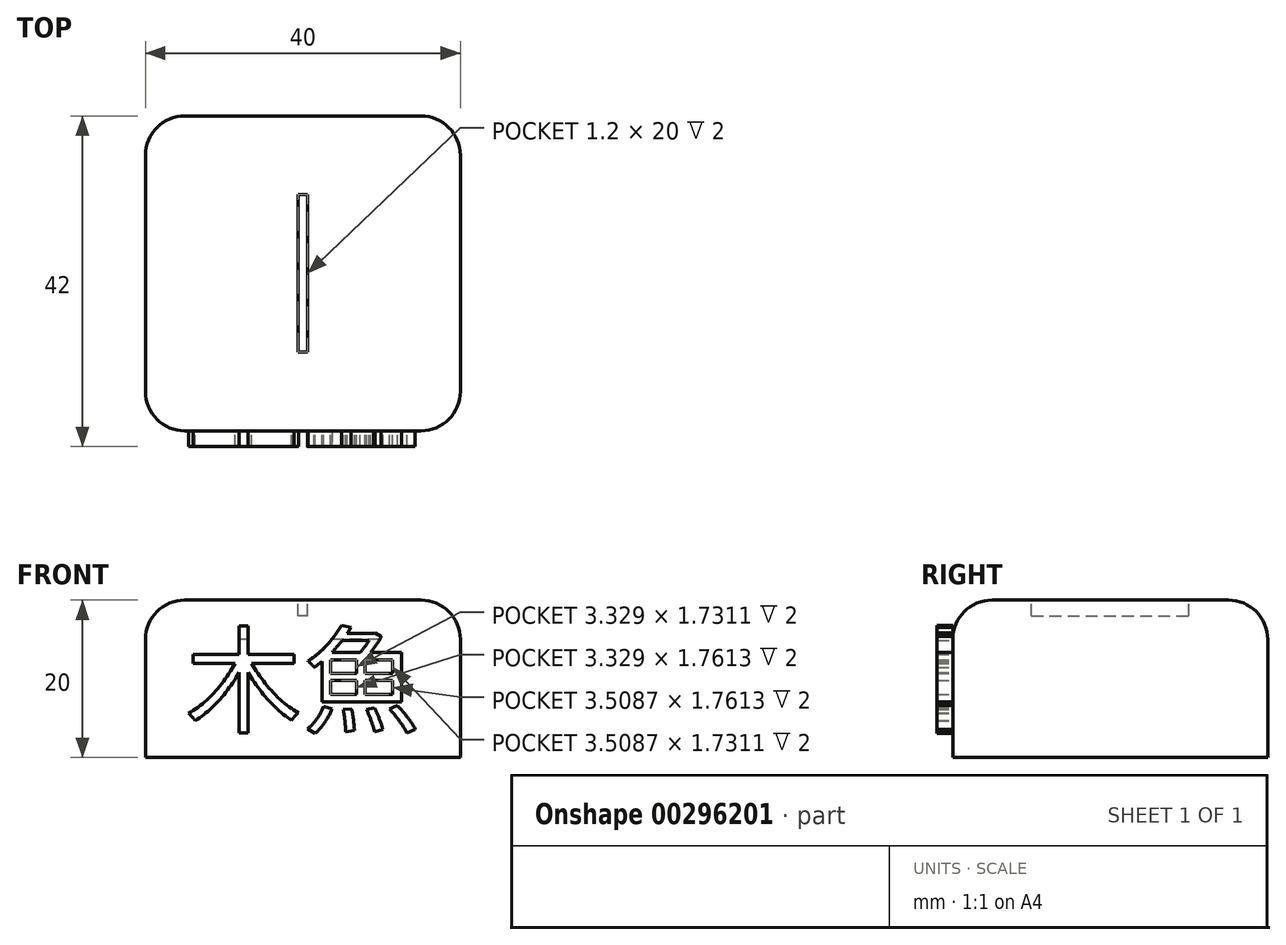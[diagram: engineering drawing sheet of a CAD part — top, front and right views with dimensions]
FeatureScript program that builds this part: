
annotation { "Feature Type Name" : "Feature", "Feature Type Description" : "" }
export const myFeature = defineFeature(function(context is Context, id is Id, definition is map)
    precondition{}
    {
        {
            var Q0;
            Q0=qCreatedBy(makeId("Top.planeOp"),FACE);
            var sketch = newSketch(context, id + "F0", { "sketchPlane" : qUnion([Q0])});
            skLineSegment(sketch, "E0.bottom", {"start": v(20, -20) * mm, "end": v(-20, -20) * mm});
            skLineSegment(sketch, "E0.top", {"start": v(20, 20) * mm, "end": v(-20, 20) * mm});
            skLineSegment(sketch, "E0.left", {"start": v(20, -20) * mm, "end": v(20, 20) * mm});
            skLineSegment(sketch, "E0.right", {"start": v(-20, -20) * mm, "end": v(-20, 20) * mm});
            skPoint(sketch, "E0.middle", {"position": v(0, 0) * mm});
            skLineSegment(sketch, "E1.bottom", {"start": v(0.6, -10) * mm, "end": v(-0.6, -10) * mm});
            skLineSegment(sketch, "E1.top", {"start": v(0.6, 10) * mm, "end": v(-0.6, 10) * mm});
            skLineSegment(sketch, "E1.left", {"start": v(0.6, -10) * mm, "end": v(0.6, 10) * mm});
            skLineSegment(sketch, "E1.right", {"start": v(-0.6, -10) * mm, "end": v(-0.6, 10) * mm});
            skSolve(sketch);
        }
        {
            var Q0;
            Q0=makeQuery(id+"F0.imprint","IMPRINT",FACE,{"disambiguationData":[TD([[makeQuery(id+"F0.imprint","IMPRINT",EDGE,{"derivedFrom":sQuery(id+"F0.wireOp",EDGE,"E0.bottom")}),-1.0]])]});
            var Q1;
            Q1=makeQuery(id+"F0.imprint","IMPRINT",FACE,{"disambiguationData":[TD([[makeQuery(id+"F0.imprint","IMPRINT",EDGE,{"derivedFrom":sQuery(id+"F0.wireOp",EDGE,"E1.bottom")}),-1.0]])]});
            extrude(context, id + "F1", {"entities" : qUnion([Q0, Q1]), "oppositeDirection" : true, "depth" : 20 * mm});
        }
        {
            var Q0;
            Q0=makeQuery(id+"F0.imprint","IMPRINT",FACE,{"disambiguationData":[TD([[makeQuery(id+"F0.imprint","IMPRINT",EDGE,{"derivedFrom":sQuery(id+"F0.wireOp",EDGE,"E1.bottom")}),-1.0]])]});
            extrude(context, id + "F2", {"entities" : qUnion([Q0]), "operationType" : NewBodyOperationType.REMOVE, "oppositeDirection" : true, "depth" : 2 * mm});
        }
        {
            var Q0;
            Q0=makeQuery(id+"F2.boolean.opBoolean","COPY",EDGE,{"derivedFrom":makeQuery(id+"F2.opExtrude","CAP_EDGE",EDGE,{"disambiguationData":[OSD([sQuery(id+"F0.wireOp",EDGE,"E1.left")])],"isStart":true})});
            var Q1;
            Q1=makeQuery(id+"F2.boolean.opBoolean","COPY",EDGE,{"derivedFrom":makeQuery(id+"F2.opExtrude","CAP_EDGE",EDGE,{"disambiguationData":[OSD([sQuery(id+"F0.wireOp",EDGE,"E1.right")])],"isStart":true})});
            var Q2;
            Q2=makeQuery(id+"F1.opExtrude","SWEPT_EDGE",EDGE,{"disambiguationData":[OSD([sQuery(id+"F0.wireOp",EDGE,"E0.bottom"),sQuery(id+"F0.wireOp",EDGE,"E0.left")])]});
            var Q3;
            Q3=makeQuery(id+"F1.opExtrude","SWEPT_EDGE",EDGE,{"disambiguationData":[OSD([sQuery(id+"F0.wireOp",EDGE,"E0.top"),sQuery(id+"F0.wireOp",EDGE,"E0.left")])]});
            var Q4;
            Q4=makeQuery(id+"F1.opExtrude","CAP_EDGE",EDGE,{"disambiguationData":[OSD([sQuery(id+"F0.wireOp",EDGE,"E0.left")])],"isStart":true});
            var Q5;
            Q5=makeQuery(id+"F1.opExtrude","SWEPT_EDGE",EDGE,{"disambiguationData":[OSD([sQuery(id+"F0.wireOp",EDGE,"E0.bottom"),sQuery(id+"F0.wireOp",EDGE,"E0.right")])]});
            var Q6;
            Q6=makeQuery(id+"F1.opExtrude","SWEPT_EDGE",EDGE,{"disambiguationData":[OSD([sQuery(id+"F0.wireOp",EDGE,"E0.top"),sQuery(id+"F0.wireOp",EDGE,"E0.right")])]});
            var Q7;
            Q7=makeQuery(id+"F1.opExtrude","CAP_EDGE",EDGE,{"disambiguationData":[OSD([sQuery(id+"F0.wireOp",EDGE,"E0.top")])],"isStart":true});
            var Q8;
            Q8=makeQuery(id+"F1.opExtrude","CAP_EDGE",EDGE,{"disambiguationData":[OSD([sQuery(id+"F0.wireOp",EDGE,"E0.right")])],"isStart":true});
            var Q9;
            Q9=makeQuery(id+"F1.opExtrude","CAP_EDGE",EDGE,{"disambiguationData":[OSD([sQuery(id+"F0.wireOp",EDGE,"E0.bottom")])],"isStart":true});
            fillet(context, id + "F3", {"entities" : qUnion([Q0, Q1, Q2, Q3, Q4, Q5, Q6, Q7, Q8, Q9]), "radius" : 5 * mm, "tangentPropagation" : true, "allowEdgeOverflow" : false});
        }
        {
            var Q0;
            Q0=makeQuery(id+"F1.opExtrude","SWEPT_FACE",FACE,{"disambiguationData":[OSD([sQuery(id+"F0.wireOp",EDGE,"E0.bottom")])]});
            var sketch = newSketch(context, id + "F4", { "sketchPlane" : qUnion([Q0])});
            skText(sketch, "E2", { "text": "木魚", "fontName": "NotoSansCJKtc-Regular.otf"});
            const initialGuessF4  = {"E2": [-0.015, -0.01575, 1, 0, 0.01075]};
            skSetInitialGuess(sketch, initialGuessF4);
            skSolve(sketch);
        }
        {
            var Q0;
            Q0=makeQuery(id+"F4.imprint","IMPRINT",FACE,{"disambiguationData":[TD([[makeQuery(id+"F4.imprint","IMPRINT",EDGE,{"derivedFrom":sQuery(id+"F4.wireOp",EDGE,"E2.sketch_text.stroke-0")}),1.0]])]});
            var Q1;
            {var subQ0=sQuery(id+"F4.wireOp",EDGE,"E2.sketch_text.stroke-3");Q1=makeQuery(id+"F4.imprint","IMPRINT",FACE,{"disambiguationData":[TD([[makeQuery(id+"F4.imprint","IMPRINT",EDGE,{"derivedFrom":subQ0}),1.0]])]});}
            var Q2;
            Q2=makeQuery(id+"F4.imprint","IMPRINT",FACE,{"disambiguationData":[TD([[makeQuery(id+"F4.imprint","IMPRINT",EDGE,{"derivedFrom":sQuery(id+"F4.wireOp",EDGE,"E2.sketch_text.stroke-18")}),1.0]])]});
            var Q3;
            {var subQ0=sQuery(id+"F4.wireOp",EDGE,"E2.sketch_text.stroke-42");Q3=makeQuery(id+"F4.imprint","IMPRINT",FACE,{"disambiguationData":[TD([[makeQuery(id+"F4.imprint","IMPRINT",EDGE,{"derivedFrom":subQ0}),1.0]])]});}
            var Q4;
            Q4=makeQuery(id+"F4.imprint","IMPRINT",FACE,{"disambiguationData":[TD([[makeQuery(id+"F4.imprint","IMPRINT",EDGE,{"derivedFrom":sQuery(id+"F4.wireOp",EDGE,"E2.sketch_text.stroke-51")}),1.0]])]});
            var Q5;
            Q5=makeQuery(id+"F4.imprint","IMPRINT",FACE,{"disambiguationData":[TD([[makeQuery(id+"F4.imprint","IMPRINT",EDGE,{"derivedFrom":sQuery(id+"F4.wireOp",EDGE,"E2.sketch_text.stroke-55")}),1.0]])]});
            var Q6;
            Q6=makeQuery(id+"F4.imprint","IMPRINT",FACE,{"disambiguationData":[TD([[makeQuery(id+"F4.imprint","IMPRINT",EDGE,{"derivedFrom":sQuery(id+"F4.wireOp",EDGE,"E2.sketch_text.stroke-59")}),1.0]])]});
            var Q7;
            Q7=makeQuery(id+"F4.imprint","IMPRINT",FACE,{"disambiguationData":[TD([[makeQuery(id+"F4.imprint","IMPRINT",EDGE,{"derivedFrom":sQuery(id+"F4.wireOp",EDGE,"E2.sketch_text.stroke-63")}),1.0]])]});
            extrude(context, id + "F5", {"entities" : qUnion([Q0, Q1, Q2, Q3, Q4, Q5, Q6, Q7]), "operationType" : NewBodyOperationType.ADD, "depth" : 2 * mm});
        }
    });
